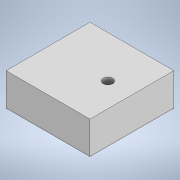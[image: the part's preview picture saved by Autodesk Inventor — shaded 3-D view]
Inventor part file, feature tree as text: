
AUTODESK INVENTOR PART (.ipt)
format: ipt  version: 2020.2 (Build 242310000, 310)  size: 183,808 bytes
history: native  units: mm
features: extrude x5, sketch x5, fillet x3
ambient origin geometry x8: Origin, YZ Plane, XZ Plane, XY Plane, X Axis, Y Axis, Z Axis, Center Point
bodies: Solide1 (feature_tree)
feature tree (13):
  extrude  "Extrusion1"  Depth=20.0mm
  extrude  "Extrusion2"  Depth=70.0mm TaperAngle=0.0deg
  extrude  "Extrusion3"  Depth=35.0mm
  extrude  "Extrusion4"  Depth=20.0mm
  fillet  "Congé3"  Radius=70.0mm
  fillet  "Congé4"  Radius=8.0mm
  extrude  "Extrusion5"  Depth=18.0mm TaperAngle=0.0deg
  fillet  "Congé5"  Radius=22.0mm
  sketch  "Esquisse1"
  sketch  "Esquisse2"
  sketch  "Esquisse3"
  sketch  "Esquisse4"
  sketch  "Esquisse5"
